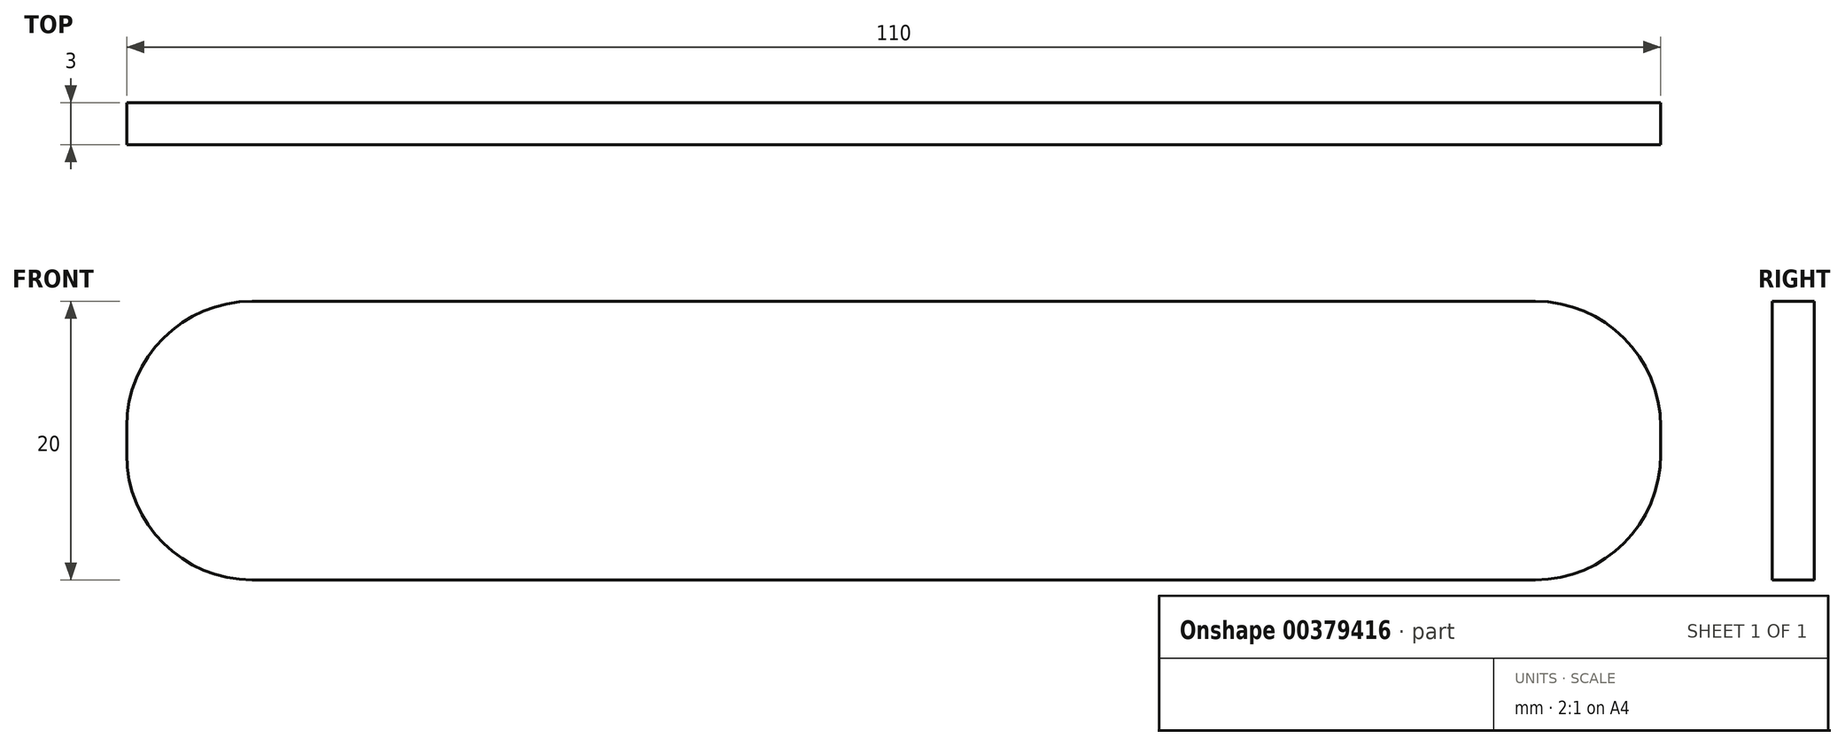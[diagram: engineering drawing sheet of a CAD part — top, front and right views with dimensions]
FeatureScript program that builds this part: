
annotation { "Feature Type Name" : "Feature", "Feature Type Description" : "" }
export const myFeature = defineFeature(function(context is Context, id is Id, definition is map)
    precondition{}
    {
        {
            var Q0;
            Q0=qCreatedBy(makeId("Front.planeOp"),FACE);
            var sketch = newSketch(context, id + "F0", { "sketchPlane" : qUnion([Q0])});
            skLineSegment(sketch, "E0.bottom", {"start": v(4.6, 0) * mm, "end": v(114.6, 0) * mm});
            skLineSegment(sketch, "E0.top", {"start": v(4.6, 20) * mm, "end": v(114.6, 20) * mm});
            skLineSegment(sketch, "E0.left", {"start": v(4.6, 0) * mm, "end": v(4.6, 20) * mm});
            skLineSegment(sketch, "E0.right", {"start": v(114.6, 0) * mm, "end": v(114.6, 20) * mm});
            skSolve(sketch);
        }
        {
            var Q0;
            Q0=makeQuery(id+"F0.imprint","IMPRINT",FACE,{"disambiguationData":[TD([[makeQuery(id+"F0.imprint","IMPRINT",EDGE,{"derivedFrom":sQuery(id+"F0.wireOp",EDGE,"E0.bottom")}),1.0]])]});
            extrude(context, id + "F1", {"entities" : qUnion([Q0]), "depth" : 3 * mm});
        }
        {
            var Q0;
            Q0=makeQuery(id+"F1.opExtrude","SWEPT_EDGE",EDGE,{"disambiguationData":[OSD([sQuery(id+"F0.wireOp",EDGE,"E0.top"),sQuery(id+"F0.wireOp",EDGE,"E0.left")])]});
            var Q1;
            Q1=makeQuery(id+"F1.opExtrude","SWEPT_EDGE",EDGE,{"disambiguationData":[OSD([sQuery(id+"F0.wireOp",EDGE,"E0.bottom"),sQuery(id+"F0.wireOp",EDGE,"E0.left")])]});
            var Q2;
            Q2=makeQuery(id+"F1.opExtrude","SWEPT_EDGE",EDGE,{"disambiguationData":[OSD([sQuery(id+"F0.wireOp",EDGE,"E0.top"),sQuery(id+"F0.wireOp",EDGE,"E0.right")])]});
            var Q3;
            Q3=makeQuery(id+"F1.opExtrude","SWEPT_EDGE",EDGE,{"disambiguationData":[OSD([sQuery(id+"F0.wireOp",EDGE,"E0.bottom"),sQuery(id+"F0.wireOp",EDGE,"E0.right")])]});
            fillet(context, id + "F2", {"entities" : qUnion([Q0, Q1, Q2, Q3]), "radius" : 9 * mm, "tangentPropagation" : true, "allowEdgeOverflow" : false});
        }
    });
